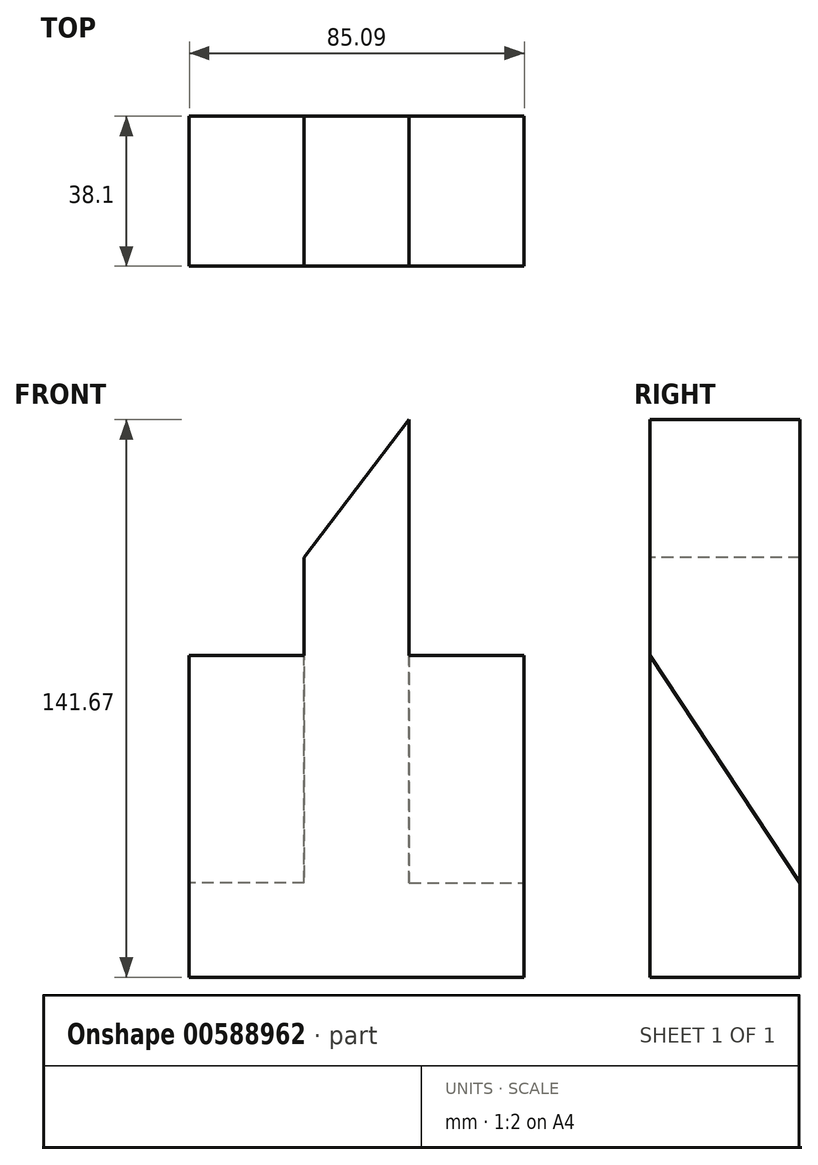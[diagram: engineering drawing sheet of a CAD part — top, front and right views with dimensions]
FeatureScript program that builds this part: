
annotation { "Feature Type Name" : "Feature", "Feature Type Description" : "" }
export const myFeature = defineFeature(function(context is Context, id is Id, definition is map)
    precondition{}
    {
        {
            var Q0;
            Q0=qCreatedBy(makeId("Top.planeOp"),FACE);
            var sketch = newSketch(context, id + "F0", { "sketchPlane" : qUnion([Q0])});
            skLineSegment(sketch, "E0", {"start": v(-59.4, 0) * mm, "end": v(-59.4, 38.1) * mm});
            skLineSegment(sketch, "E1", {"start": v(-59.4, 38.1) * mm, "end": v(-14.95, 38.1) * mm});
            skLineSegment(sketch, "E2", {"start": v(-59.4, 0) * mm, "end": v(-14.95, 0) * mm});
            skLineSegment(sketch, "E3", {"start": v(-14.95, 0) * mm, "end": v(-14.95, 38.1) * mm});
            skSolve(sketch);
        }
        {
            var Q0;
            Q0=makeQuery(id+"F0.imprint","IMPRINT",FACE,{"disambiguationData":[TD([[makeQuery(id+"F0.imprint","IMPRINT",EDGE,{"derivedFrom":sQuery(id+"F0.wireOp",EDGE,"E0")}),-1.0]])]});
            extrude(context, id + "F1", {"entities" : qUnion([Q0]), "depth" : 25.4 * mm, "offsetDistance" : 25.4 * mm});
        }
        {
            var Q0;
            Q0=makeQuery(id+"F1.opExtrude","CAP_FACE",FACE,{"disambiguationData":[OSD([sQuery(id+"F0.wireOp",EDGE,"E0"),sQuery(id+"F0.wireOp",EDGE,"E1"),sQuery(id+"F0.wireOp",EDGE,"E2"),sQuery(id+"F0.wireOp",EDGE,"E3")])],"isStart":true});
            extrude(context, id + "F2", {"entities" : qUnion([Q0]), "operationType" : NewBodyOperationType.ADD, "depth" : 56.4 * mm, "offsetDistance" : 25.4 * mm});
        }
        {
            var Q0;
            {var subQ0=sQuery(id+"F0.wireOp",EDGE,"E0");Q0=makeQuery(id+"F2.boolean.opBoolean","MERGE",FACE,{"derivedFrom":[makeQuery(id+"F1.opExtrude","SWEPT_FACE",FACE,{"disambiguationData":[OSD([subQ0])]}),makeQuery(id+"F2.opExtrude","SWEPT_FACE",FACE,{"disambiguationData":[OSD([subQ0])]})]});}
            extrude(context, id + "F3", {"entities" : qUnion([Q0]), "operationType" : NewBodyOperationType.ADD, "oppositeDirection" : true, "depth" : 85.1 * mm, "offsetDistance" : 25.4 * mm});
        }
        {
            var Q0;
            {var subQ0=sQuery(id+"F0.wireOp",EDGE,"E0");Q0=makeQuery(id+"F2.boolean.opBoolean","MERGE",FACE,{"derivedFrom":[makeQuery(id+"F1.opExtrude","SWEPT_FACE",FACE,{"disambiguationData":[OSD([subQ0])]}),makeQuery(id+"F2.opExtrude","SWEPT_FACE",FACE,{"disambiguationData":[OSD([subQ0])]})]});}
            var sketch = newSketch(context, id + "F4", { "sketchPlane" : qUnion([Q0])});
            skLineSegment(sketch, "E4", {"start": v(-38.1, -32.36) * mm, "end": v(0, 25.4) * mm});
            skSolve(sketch);
        }
        {
            var Q0;
            Q0=makeQuery(id+"F3.opExtrude","CAP_FACE",FACE,{"disambiguationData":[OSD([sQuery(id+"F0.wireOp",EDGE,"E0")])],"isStart":false});
            var sketch = newSketch(context, id + "F5", { "sketchPlane" : qUnion([Q0])});
            skLineSegment(sketch, "E5", {"start": v(38.1, -32.4) * mm, "end": v(0, 25.4) * mm});
            skSolve(sketch);
        }
        {
            var Q0;
            {var subQ0=sQuery(id+"F5.wireOp",EDGE,"E5");Q0=makeQuery(id+"F5.imprint","IMPRINT",FACE,{"disambiguationData":[TD([[makeQuery(id+"F5.imprint","IMPRINT",EDGE,{"derivedFrom":subQ0}),-1.0]])]});}
            extrude(context, id + "F6", {"entities" : qUnion([Q0]), "operationType" : NewBodyOperationType.REMOVE, "oppositeDirection" : true, "depth" : 29.2 * mm, "offsetDistance" : 25.4 * mm});
        }
        {
            var Q0;
            {var subQ0=sQuery(id+"F4.wireOp",EDGE,"E4");Q0=makeQuery(id+"F4.imprint","IMPRINT",FACE,{"disambiguationData":[TD([[makeQuery(id+"F4.imprint","IMPRINT",EDGE,{"derivedFrom":subQ0}),1.0]])]});}
            extrude(context, id + "F7", {"entities" : qUnion([Q0]), "operationType" : NewBodyOperationType.REMOVE, "oppositeDirection" : true, "depth" : 29.2 * mm, "offsetDistance" : 25.4 * mm});
        }
        {
            var Q0;
            {var subQ0=sQuery(id+"F0.wireOp",EDGE,"E0");Q0=makeQuery(id+"F3.boolean.opBoolean","MERGE",FACE,{"derivedFrom":[makeQuery(id+"F1.opExtrude","CAP_FACE",FACE,{"disambiguationData":[OSD([subQ0,sQuery(id+"F0.wireOp",EDGE,"E1"),sQuery(id+"F0.wireOp",EDGE,"E2"),sQuery(id+"F0.wireOp",EDGE,"E3")])],"isStart":false}),makeQuery(id+"F3.opExtrude","SWEPT_FACE",FACE,{"disambiguationData":[OSD([subQ0]),TDD([makeQuery(id+"F1.opExtrude","CAP_EDGE",EDGE,{"disambiguationData":[OSD([subQ0])],"isStart":false})])]})]});}
            extrude(context, id + "F8", {"entities" : qUnion([Q0]), "operationType" : NewBodyOperationType.ADD, "depth" : 64.52 * mm, "offsetDistance" : 25.4 * mm});
        }
        {
            var Q0;
            {var subQ0=sQuery(id+"F0.wireOp",EDGE,"E0");Q0=makeQuery(id+"F8.boolean.opBoolean","MERGE",FACE,{"derivedFrom":[makeQuery(id+"F7.boolean.opBoolean","COPY",FACE,{"derivedFrom":makeQuery(id+"F7.opExtrude","CAP_FACE",FACE,{"disambiguationData":[OSD([subQ0,sQuery(id+"F0.wireOp",EDGE,"E1"),sQuery(id+"F4.wireOp",EDGE,"E4")])],"isStart":false})}),makeQuery(id+"F8.opExtrude","SWEPT_FACE",FACE,{"disambiguationData":[OSD([subQ0]),TDD([makeQuery(id+"F7.boolean.opBoolean","COPY",EDGE,{"derivedFrom":makeQuery(id+"F7.opExtrude","CAP_EDGE",EDGE,{"disambiguationData":[OSD([subQ0])],"isStart":false})})])]})]});}
            var sketch = newSketch(context, id + "F9", { "sketchPlane" : qUnion([Q0])});
            skLineSegment(sketch, "E6", {"start": v(-38.1, 39.81) * mm, "end": v(0, 89.92) * mm});
            skSolve(sketch);
        }
        {
            var Q0;
            {var subQ0=sQuery(id+"F9.wireOp",EDGE,"E6");Q0=makeQuery(id+"F9.imprint","IMPRINT",FACE,{"disambiguationData":[TD([[makeQuery(id+"F9.imprint","IMPRINT",EDGE,{"derivedFrom":subQ0}),1.0]])]});}
            extrude(context, id + "F10", {"entities" : qUnion([Q0]), "operationType" : NewBodyOperationType.REMOVE, "oppositeDirection" : true, "depth" : 25.4 * mm, "offsetDistance" : 25.4 * mm});
        }
        {
            var Q0;
            Q0=makeQuery(id+"F10.boolean.opBoolean","COPY",FACE,{"derivedFrom":makeQuery(id+"F10.opExtrude","CAP_FACE",FACE,{"disambiguationData":[OSD([sQuery(id+"F0.wireOp",EDGE,"E0"),sQuery(id+"F0.wireOp",EDGE,"E1"),sQuery(id+"F9.wireOp",EDGE,"E6")])],"isStart":false})});
            extrude(context, id + "F11", {"entities" : qUnion([Q0]), "operationType" : NewBodyOperationType.REMOVE, "oppositeDirection" : true, "depth" : 25.4 * mm, "offsetDistance" : 25.4 * mm});
        }
    });
